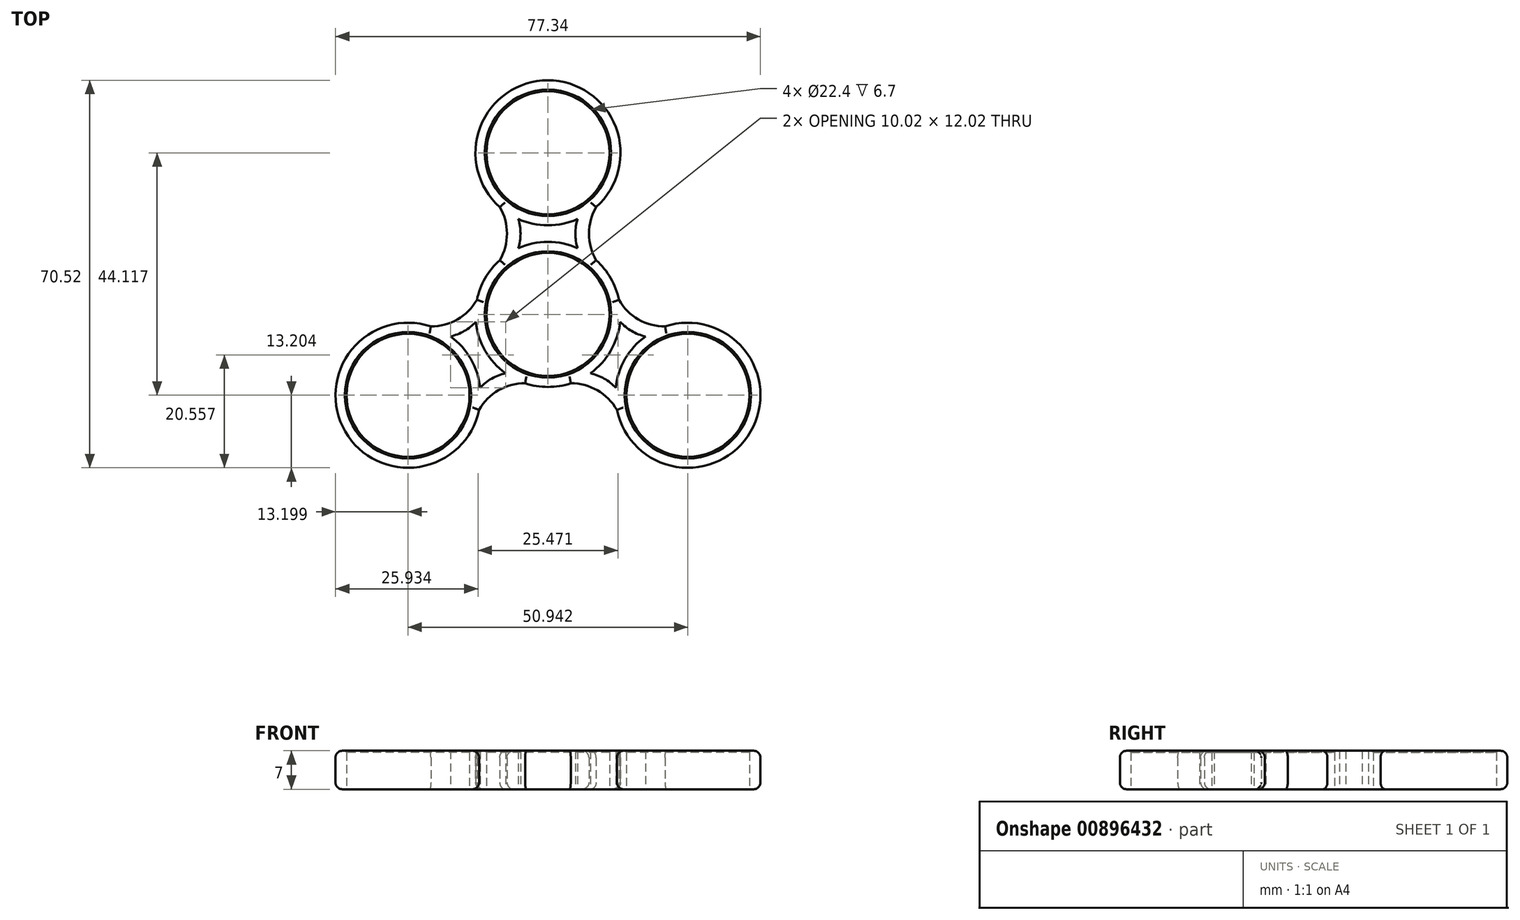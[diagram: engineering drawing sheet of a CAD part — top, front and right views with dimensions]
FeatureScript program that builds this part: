
annotation { "Feature Type Name" : "Feature", "Feature Type Description" : "" }
export const myFeature = defineFeature(function(context is Context, id is Id, definition is map)
    precondition{}
    {
        {
            var Q0;
            Q0=qCreatedBy(makeId("Top.planeOp"),FACE);
            var sketch = newSketch(context, id + "F0", { "sketchPlane" : qUnion([Q0])});
            skCircle(sketch, "E0", {"center": v(0, 0) * mm, "radius": 11.2 * mm});
            skArc(sketch, "E1", {"start": v(5.4, 12.04) * mm, "mid": v(0, 13.2) * mm, "end": v(-5.4, 12.04) * mm});
            skArc(sketch, "E2", {"start": v(-5.4, 17.37) * mm, "mid": v(0, 16.21) * mm, "end": v(5.4, 17.37) * mm});
            skPoint(sketch, "E3.center", {"position": v(1.87, -1.79) * mm});
            skPoint(sketch, "E4.endSnap0", {"position": v(0, 14.7) * mm});
            skPoint(sketch, "E5.startSnap0", {"position": v(7.46, 14.7) * mm});
            skPoint(sketch, "E5.endSnap0", {"position": v(7.46, 14.7) * mm});
            skArc(sketch, "E6", {"start": v(8.77, 19.55) * mm, "mid": v(7.46, 14.7) * mm, "end": v(8.77, 9.86) * mm});
            skArc(sketch, "E7", {"start": v(5.4, 17.37) * mm, "mid": v(5, 14.7) * mm, "end": v(5.4, 12.04) * mm});
            skArc(sketch, "E8.MirrorCS", {"start": v(-5.4, 17.37) * mm, "mid": v(-5, 14.7) * mm, "end": v(-5.4, 12.04) * mm});
            skArc(sketch, "E9.MirrorCS", {"start": v(-8.77, 19.55) * mm, "mid": v(-7.46, 14.7) * mm, "end": v(-8.77, 9.86) * mm});
            skPoint(sketch, "E10.end.orphan", {"position": v(13.2, 0) * mm});
            skPoint(sketch, "E10.start.orphan", {"position": v(13.2, 29.41) * mm});
            skArc(sketch, "E11.1.0", {"start": v(-12.34, -13.37) * mm, "mid": v(-10.24, -11.68) * mm, "end": v(-7.73, -10.7) * mm});
            skArc(sketch, "E11.1.1", {"start": v(-12.54, -17.37) * mm, "mid": v(-9, -13.8) * mm, "end": v(-4.15, -12.53) * mm});
            skArc(sketch, "E11.1.2", {"start": v(-21.32, -2.18) * mm, "mid": v(-36.9, -21.3) * mm, "end": v(-12.54, -17.37) * mm});
            skCircle(sketch, "E11.1.3", {"center": v(-25.47, -14.7) * mm, "radius": 11.2 * mm});
            skArc(sketch, "E11.1.4", {"start": v(-17.74, -4) * mm, "mid": v(-15.23, -3.03) * mm, "end": v(-13.13, -1.34) * mm});
            skArc(sketch, "E11.1.5", {"start": v(-21.32, -2.18) * mm, "mid": v(-16.46, -0.9) * mm, "end": v(-12.93, 2.67) * mm});
            skArc(sketch, "E11.2.0", {"start": v(17.74, -4) * mm, "mid": v(15.23, -3.03) * mm, "end": v(13.13, -1.34) * mm});
            skArc(sketch, "E11.2.1", {"start": v(21.32, -2.18) * mm, "mid": v(16.46, -0.9) * mm, "end": v(12.93, 2.67) * mm});
            skArc(sketch, "E11.2.2", {"start": v(12.54, -17.37) * mm, "mid": v(36.9, -21.3) * mm, "end": v(21.32, -2.18) * mm});
            skCircle(sketch, "E11.2.3", {"center": v(25.47, -14.7) * mm, "radius": 11.2 * mm});
            skArc(sketch, "E11.2.4", {"start": v(12.34, -13.37) * mm, "mid": v(10.24, -11.68) * mm, "end": v(7.73, -10.7) * mm});
            skArc(sketch, "E11.2.5", {"start": v(12.54, -17.37) * mm, "mid": v(9, -13.8) * mm, "end": v(4.15, -12.53) * mm});
            skLineSegment(sketch, "E12", {"start": v(10.7, 7.72) * mm, "end": v(9.08, 6.55) * mm, "construction": true});
            skPoint(sketch, "E13.endSnap0", {"position": v(23.13, 38.87) * mm});
            skCircle(sketch, "E14", {"center": v(0, 29.41) * mm, "radius": 11.2 * mm});
            skArc(sketch, "E15.trimOffspring", {"start": v(8.77, 19.55) * mm, "mid": v(0, 42.61) * mm, "end": v(-8.77, 19.55) * mm});
            skArc(sketch, "E16.trimOffspring", {"start": v(-8.77, 9.86) * mm, "mid": v(-11.43, 6.6) * mm, "end": v(-12.93, 2.67) * mm});
            skArc(sketch, "E17.trimOffspring", {"start": v(-13.13, -1.34) * mm, "mid": v(-11.43, -6.6) * mm, "end": v(-7.73, -10.7) * mm});
            skArc(sketch, "E18.trimOffspring", {"start": v(-12.34, -13.37) * mm, "mid": v(-14.04, -8.1) * mm, "end": v(-17.74, -4) * mm});
            skArc(sketch, "E19.trimOffspring", {"start": v(-4.15, -12.53) * mm, "mid": v(0, -13.2) * mm, "end": v(4.15, -12.53) * mm});
            skArc(sketch, "E20.trimOffspring", {"start": v(7.73, -10.7) * mm, "mid": v(11.43, -6.6) * mm, "end": v(13.13, -1.34) * mm});
            skArc(sketch, "E21.trimOffspring", {"start": v(17.74, -4) * mm, "mid": v(14.04, -8.1) * mm, "end": v(12.34, -13.37) * mm});
            skArc(sketch, "E22.trimOffspring", {"start": v(12.93, 2.67) * mm, "mid": v(11.43, 6.6) * mm, "end": v(8.77, 9.86) * mm});
            skPoint(sketch, "E23.orphan", {"position": v(25.47, -1.5) * mm});
            skPoint(sketch, "E24.start.orphan", {"position": v(19.34, 13.95) * mm});
            skPoint(sketch, "E25.end.orphan", {"position": v(25.47, 29.41) * mm});
            skPoint(sketch, "E25.start.orphan", {"position": v(25.47, 13.95) * mm});
            skSolve(sketch);
        }
        {
            var Q0;
            Q0=makeQuery(id+"F0.imprint","IMPRINT",FACE,{"disambiguationData":[TD([[makeQuery(id+"F0.imprint","IMPRINT",EDGE,{"derivedFrom":sQuery(id+"F0.wireOp",EDGE,"E0")}),-1.0]])]});
            extrude(context, id + "F1", {"entities" : qUnion([Q0]), "depth" : 7 * mm, "offsetDistance" : 25 * mm});
        }
        {
            var Q0;
            Q0=makeQuery(id+"F1.opExtrude","CAP_EDGE",EDGE,{"disambiguationData":[OSD([sQuery(id+"F0.wireOp",EDGE,"E11.1.2")])],"isStart":false});
            var Q1;
            Q1=makeQuery(id+"F1.opExtrude","CAP_EDGE",EDGE,{"disambiguationData":[OSD([sQuery(id+"F0.wireOp",EDGE,"E11.1.1")])],"isStart":false});
            var Q2;
            Q2=makeQuery(id+"F1.opExtrude","CAP_EDGE",EDGE,{"disambiguationData":[OSD([sQuery(id+"F0.wireOp",EDGE,"E19.trimOffspring")])],"isStart":false});
            var Q3;
            Q3=makeQuery(id+"F1.opExtrude","CAP_EDGE",EDGE,{"disambiguationData":[OSD([sQuery(id+"F0.wireOp",EDGE,"E11.2.5")])],"isStart":false});
            var Q4;
            Q4=makeQuery(id+"F1.opExtrude","CAP_EDGE",EDGE,{"disambiguationData":[OSD([sQuery(id+"F0.wireOp",EDGE,"E11.2.2")])],"isStart":false});
            var Q5;
            Q5=makeQuery(id+"F1.opExtrude","CAP_EDGE",EDGE,{"disambiguationData":[OSD([sQuery(id+"F0.wireOp",EDGE,"E11.2.1")])],"isStart":false});
            var Q6;
            Q6=makeQuery(id+"F1.opExtrude","CAP_EDGE",EDGE,{"disambiguationData":[OSD([sQuery(id+"F0.wireOp",EDGE,"E22.trimOffspring")])],"isStart":false});
            var Q7;
            Q7=makeQuery(id+"F1.opExtrude","CAP_EDGE",EDGE,{"disambiguationData":[OSD([sQuery(id+"F0.wireOp",EDGE,"E6")])],"isStart":false});
            var Q8;
            Q8=makeQuery(id+"F1.opExtrude","CAP_EDGE",EDGE,{"disambiguationData":[OSD([sQuery(id+"F0.wireOp",EDGE,"E15.trimOffspring")])],"isStart":false});
            var Q9;
            Q9=makeQuery(id+"F1.opExtrude","CAP_EDGE",EDGE,{"disambiguationData":[OSD([sQuery(id+"F0.wireOp",EDGE,"E9.MirrorCS")])],"isStart":false});
            var Q10;
            Q10=makeQuery(id+"F1.opExtrude","CAP_EDGE",EDGE,{"disambiguationData":[OSD([sQuery(id+"F0.wireOp",EDGE,"E16.trimOffspring")])],"isStart":false});
            var Q11;
            Q11=makeQuery(id+"F1.opExtrude","CAP_EDGE",EDGE,{"disambiguationData":[OSD([sQuery(id+"F0.wireOp",EDGE,"E11.1.5")])],"isStart":false});
            var Q12;
            Q12=makeQuery(id+"F1.opExtrude","CAP_EDGE",EDGE,{"disambiguationData":[OSD([sQuery(id+"F0.wireOp",EDGE,"E15.trimOffspring")])],"isStart":true});
            var Q13;
            Q13=makeQuery(id+"F1.opExtrude","CAP_EDGE",EDGE,{"disambiguationData":[OSD([sQuery(id+"F0.wireOp",EDGE,"E9.MirrorCS")])],"isStart":true});
            var Q14;
            Q14=makeQuery(id+"F1.opExtrude","CAP_EDGE",EDGE,{"disambiguationData":[OSD([sQuery(id+"F0.wireOp",EDGE,"E16.trimOffspring")])],"isStart":true});
            var Q15;
            Q15=makeQuery(id+"F1.opExtrude","CAP_EDGE",EDGE,{"disambiguationData":[OSD([sQuery(id+"F0.wireOp",EDGE,"E11.1.5")])],"isStart":true});
            var Q16;
            Q16=makeQuery(id+"F1.opExtrude","CAP_EDGE",EDGE,{"disambiguationData":[OSD([sQuery(id+"F0.wireOp",EDGE,"E11.1.2")])],"isStart":true});
            var Q17;
            Q17=makeQuery(id+"F1.opExtrude","CAP_EDGE",EDGE,{"disambiguationData":[OSD([sQuery(id+"F0.wireOp",EDGE,"E11.1.1")])],"isStart":true});
            var Q18;
            Q18=makeQuery(id+"F1.opExtrude","CAP_EDGE",EDGE,{"disambiguationData":[OSD([sQuery(id+"F0.wireOp",EDGE,"E19.trimOffspring")])],"isStart":true});
            var Q19;
            Q19=makeQuery(id+"F1.opExtrude","CAP_EDGE",EDGE,{"disambiguationData":[OSD([sQuery(id+"F0.wireOp",EDGE,"E11.2.5")])],"isStart":true});
            var Q20;
            Q20=makeQuery(id+"F1.opExtrude","CAP_EDGE",EDGE,{"disambiguationData":[OSD([sQuery(id+"F0.wireOp",EDGE,"E11.2.2")])],"isStart":true});
            var Q21;
            Q21=makeQuery(id+"F1.opExtrude","CAP_EDGE",EDGE,{"disambiguationData":[OSD([sQuery(id+"F0.wireOp",EDGE,"E11.2.1")])],"isStart":true});
            var Q22;
            Q22=makeQuery(id+"F1.opExtrude","CAP_EDGE",EDGE,{"disambiguationData":[OSD([sQuery(id+"F0.wireOp",EDGE,"E22.trimOffspring")])],"isStart":true});
            var Q23;
            Q23=makeQuery(id+"F1.opExtrude","CAP_EDGE",EDGE,{"disambiguationData":[OSD([sQuery(id+"F0.wireOp",EDGE,"E6")])],"isStart":true});
            fillet(context, id + "F2", {"entities" : qUnion([Q0, Q1, Q2, Q3, Q4, Q5, Q6, Q7, Q8, Q9, Q10, Q11, Q12, Q13, Q14, Q15, Q16, Q17, Q18, Q19, Q20, Q21, Q22, Q23]), "radius" : 1.25 * mm, "tangentPropagation" : true, "allowEdgeOverflow" : false});
        }
        {
            var Q0;
            Q0=makeQuery(id+"F1.opExtrude","CAP_EDGE",EDGE,{"disambiguationData":[OSD([sQuery(id+"F0.wireOp",EDGE,"E11.2.3")])],"isStart":false});
            var Q1;
            Q1=makeQuery(id+"F1.opExtrude","CAP_EDGE",EDGE,{"disambiguationData":[OSD([sQuery(id+"F0.wireOp",EDGE,"E0")])],"isStart":false});
            var Q2;
            Q2=makeQuery(id+"F1.opExtrude","CAP_EDGE",EDGE,{"disambiguationData":[OSD([sQuery(id+"F0.wireOp",EDGE,"E11.1.3")])],"isStart":false});
            var Q3;
            Q3=makeQuery(id+"F1.opExtrude","CAP_EDGE",EDGE,{"disambiguationData":[OSD([sQuery(id+"F0.wireOp",EDGE,"E14")])],"isStart":false});
            chamfer(context, id + "F3", {"entities" : qUnion([Q0, Q1, Q2, Q3]), "width" : .3 * mm, "tangentPropagation" : true});
        }
    });
